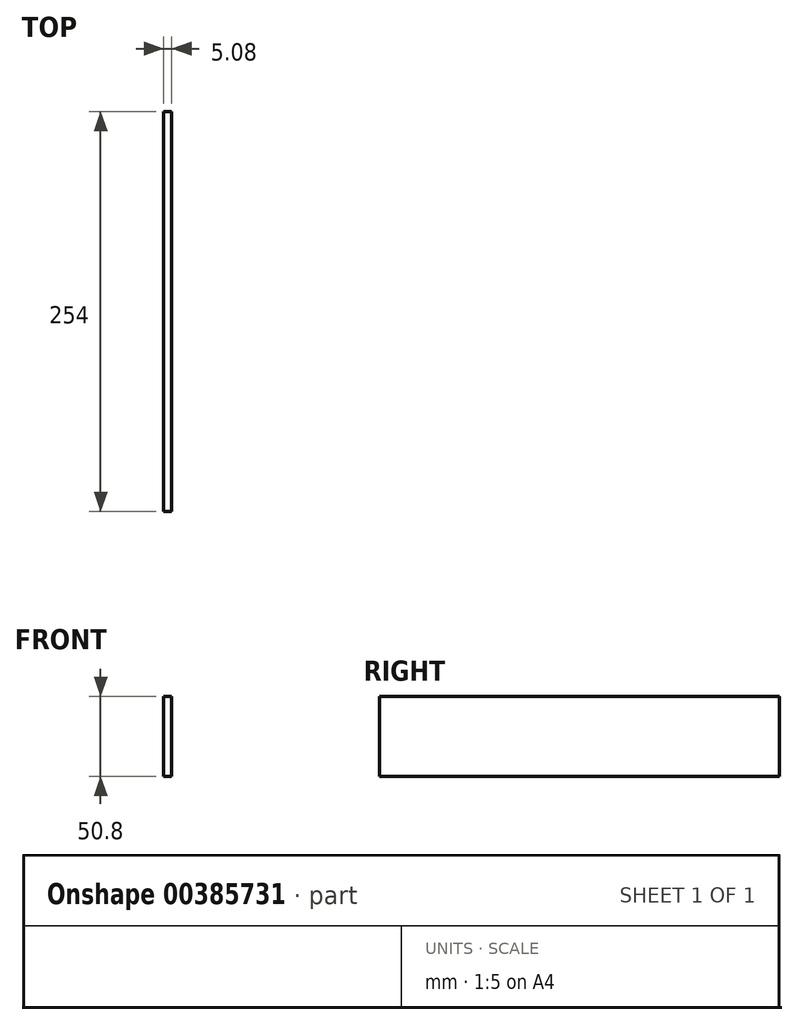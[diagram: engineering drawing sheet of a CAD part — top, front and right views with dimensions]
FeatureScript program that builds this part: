
annotation { "Feature Type Name" : "Feature", "Feature Type Description" : "" }
export const myFeature = defineFeature(function(context is Context, id is Id, definition is map)
    precondition{}
    {
        {
            var Q0;
            Q0=qCreatedBy(makeId("Front.planeOp"),FACE);
            var sketch = newSketch(context, id + "F0", { "sketchPlane" : qUnion([Q0])});
            skLineSegment(sketch, "E0.bottom", {"start": v(-2.54, 25.4) * mm, "end": v(2.54, 25.4) * mm});
            skLineSegment(sketch, "E0.top", {"start": v(-2.54, -25.4) * mm, "end": v(2.54, -25.4) * mm});
            skLineSegment(sketch, "E0.left", {"start": v(-2.54, 25.4) * mm, "end": v(-2.54, -25.4) * mm});
            skLineSegment(sketch, "E0.right", {"start": v(2.54, 25.4) * mm, "end": v(2.54, -25.4) * mm});
            skPoint(sketch, "E0.middle", {"position": v(0, 0) * mm});
            skSolve(sketch);
        }
        {
            var Q0;
            Q0 = qSketchRegion(id + "F0", true);
            extrude(context, id + "F1", {"entities" : qUnion([Q0]), "depth" : 254 * mm});
        }
    });
